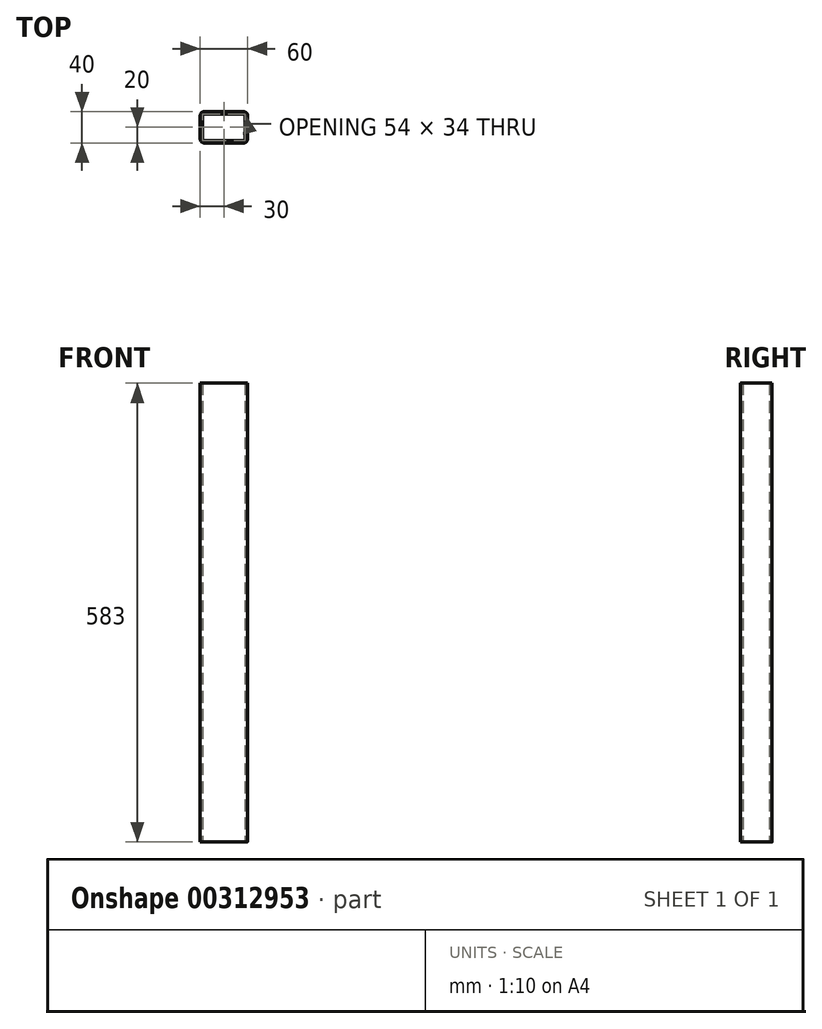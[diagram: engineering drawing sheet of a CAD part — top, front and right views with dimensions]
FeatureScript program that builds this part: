
annotation { "Feature Type Name" : "Feature", "Feature Type Description" : "" }
export const myFeature = defineFeature(function(context is Context, id is Id, definition is map)
    precondition{}
    {
        {
            var Q0;
            Q0=qCreatedBy(makeId("Top.planeOp"),FACE);
            var sketch = newSketch(context, id + "F0", { "sketchPlane" : qUnion([Q0])});
            skLineSegment(sketch, "E0.bottom", {"start": v(25, 20) * mm, "end": v(-25, 20) * mm});
            skLineSegment(sketch, "E0.top", {"start": v(25, -20) * mm, "end": v(-25, -20) * mm});
            skLineSegment(sketch, "E0.left", {"start": v(30, 15) * mm, "end": v(30, -15) * mm});
            skLineSegment(sketch, "E0.right", {"start": v(-30, 15) * mm, "end": v(-30, -15) * mm});
            skPoint(sketch, "E0.middle", {"position": v(0, 0) * mm});
            skLineSegment(sketch, "E1.0", {"start": v(25, 17) * mm, "end": v(-25, 17) * mm});
            skLineSegment(sketch, "E2.0", {"start": v(27, 15) * mm, "end": v(27, -15) * mm});
            skLineSegment(sketch, "E3.0", {"start": v(25, -17) * mm, "end": v(-25, -17) * mm});
            skLineSegment(sketch, "E4.0", {"start": v(-27, 15) * mm, "end": v(-27, -15) * mm});
            skPoint(sketch, "E5.visualSharp", {"position": v(-30, 20) * mm});
            skArc(sketch, "E5.filletArc", {"start": v(-25, 20) * mm, "mid": v(-28.54, 18.54) * mm, "end": v(-30, 15) * mm});
            skPoint(sketch, "E6.visualSharp", {"position": v(30, 20) * mm});
            skArc(sketch, "E6.filletArc", {"start": v(30, 15) * mm, "mid": v(28.54, 18.54) * mm, "end": v(25, 20) * mm});
            skPoint(sketch, "E7.visualSharp", {"position": v(30, -20) * mm});
            skArc(sketch, "E7.filletArc", {"start": v(25, -20) * mm, "mid": v(28.54, -18.54) * mm, "end": v(30, -15) * mm});
            skPoint(sketch, "E8.visualSharp", {"position": v(-30, -20) * mm});
            skArc(sketch, "E8.filletArc", {"start": v(-30, -15) * mm, "mid": v(-28.54, -18.54) * mm, "end": v(-25, -20) * mm});
            skPoint(sketch, "E9.visualSharp", {"position": v(-27, 17) * mm});
            skArc(sketch, "E9.filletArc", {"start": v(-25, 17) * mm, "mid": v(-26.41, 16.41) * mm, "end": v(-27, 15) * mm});
            skPoint(sketch, "E10.visualSharp", {"position": v(27, 17) * mm});
            skArc(sketch, "E10.filletArc", {"start": v(27, 15) * mm, "mid": v(26.41, 16.41) * mm, "end": v(25, 17) * mm});
            skPoint(sketch, "E11.visualSharp", {"position": v(27, -17) * mm});
            skArc(sketch, "E11.filletArc", {"start": v(25, -17) * mm, "mid": v(26.41, -16.41) * mm, "end": v(27, -15) * mm});
            skPoint(sketch, "E12.visualSharp", {"position": v(-27, -17) * mm});
            skArc(sketch, "E12.filletArc", {"start": v(-27, -15) * mm, "mid": v(-26.41, -16.41) * mm, "end": v(-25, -17) * mm});
            skSolve(sketch);
        }
        {
            var Q0;
            Q0=qSketchRegion(id+"F0",true);
            extrude(context, id + "F1", {"entities" : qUnion([Q0]), "depth" : 583 * mm});
        }
    });
